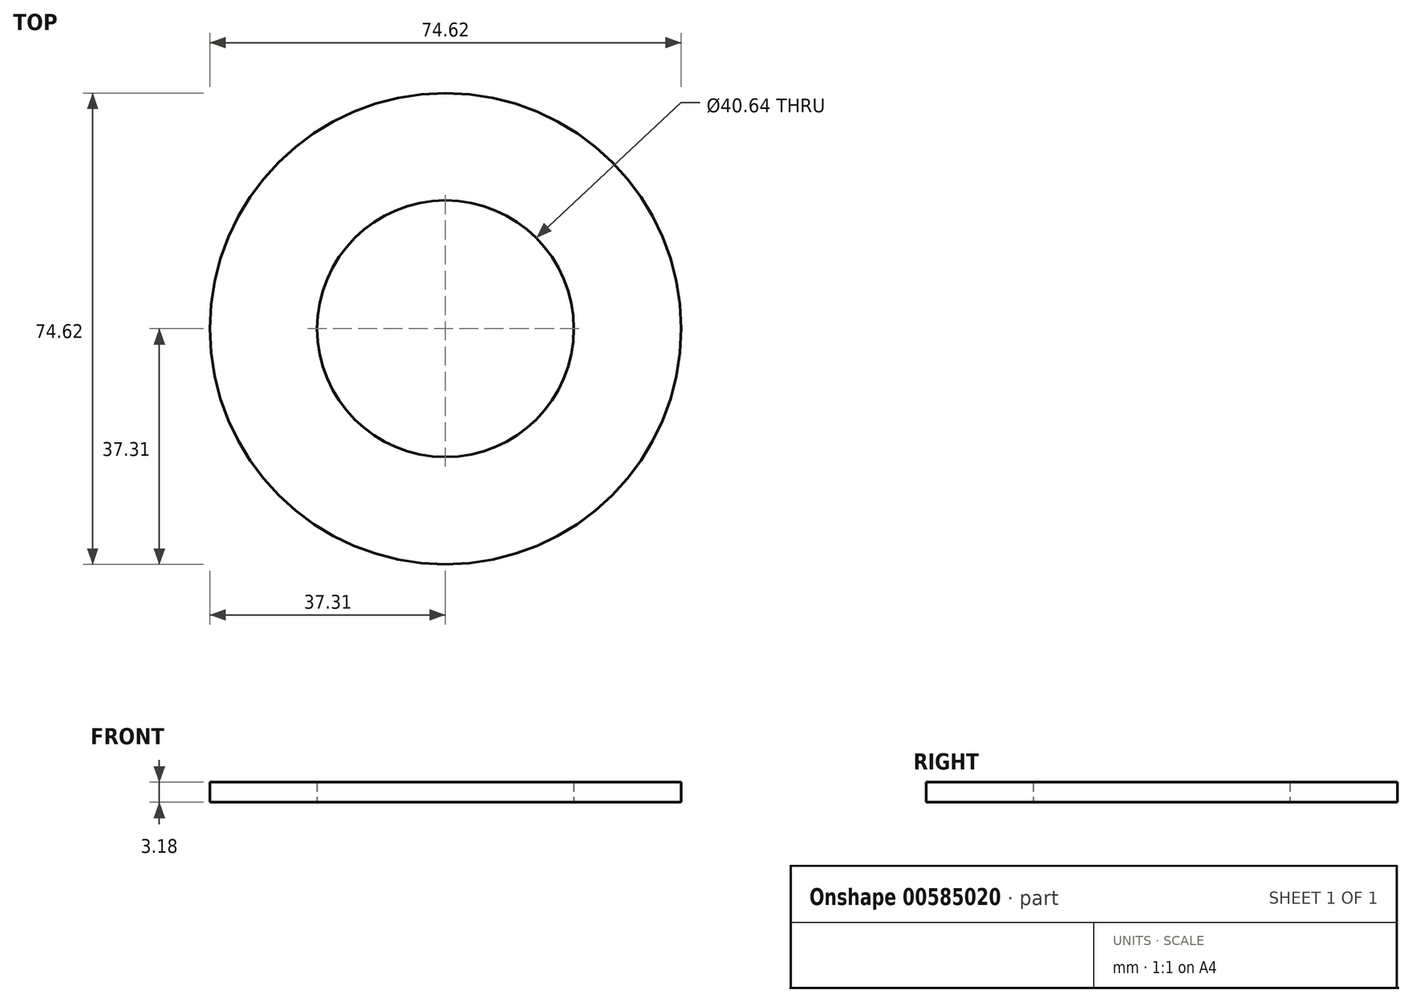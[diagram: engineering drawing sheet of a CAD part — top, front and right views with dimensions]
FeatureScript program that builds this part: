
annotation { "Feature Type Name" : "Feature", "Feature Type Description" : "" }
export const myFeature = defineFeature(function(context is Context, id is Id, definition is map)
    precondition{}
    {
        {
            var Q0;
            Q0=qCreatedBy(makeId("Top.planeOp"),FACE);
            var sketch = newSketch(context, id + "F0", { "sketchPlane" : qUnion([Q0])});
            skCircle(sketch, "E0", {"center": v(0, 0) * mm, "radius": 20.32 * mm});
            skCircle(sketch, "E1", {"center": v(0, 0) * mm, "radius": 37.3 * mm});
            skSolve(sketch);
        }
        {
            var Q0;
            Q0 = qSketchRegion(id + "F0", true);
            extrude(context, id + "F1", {"entities" : qUnion([Q0]), "depth" : 3.17 * mm, "offsetDistance" : 25.4 * mm});
        }
    });
